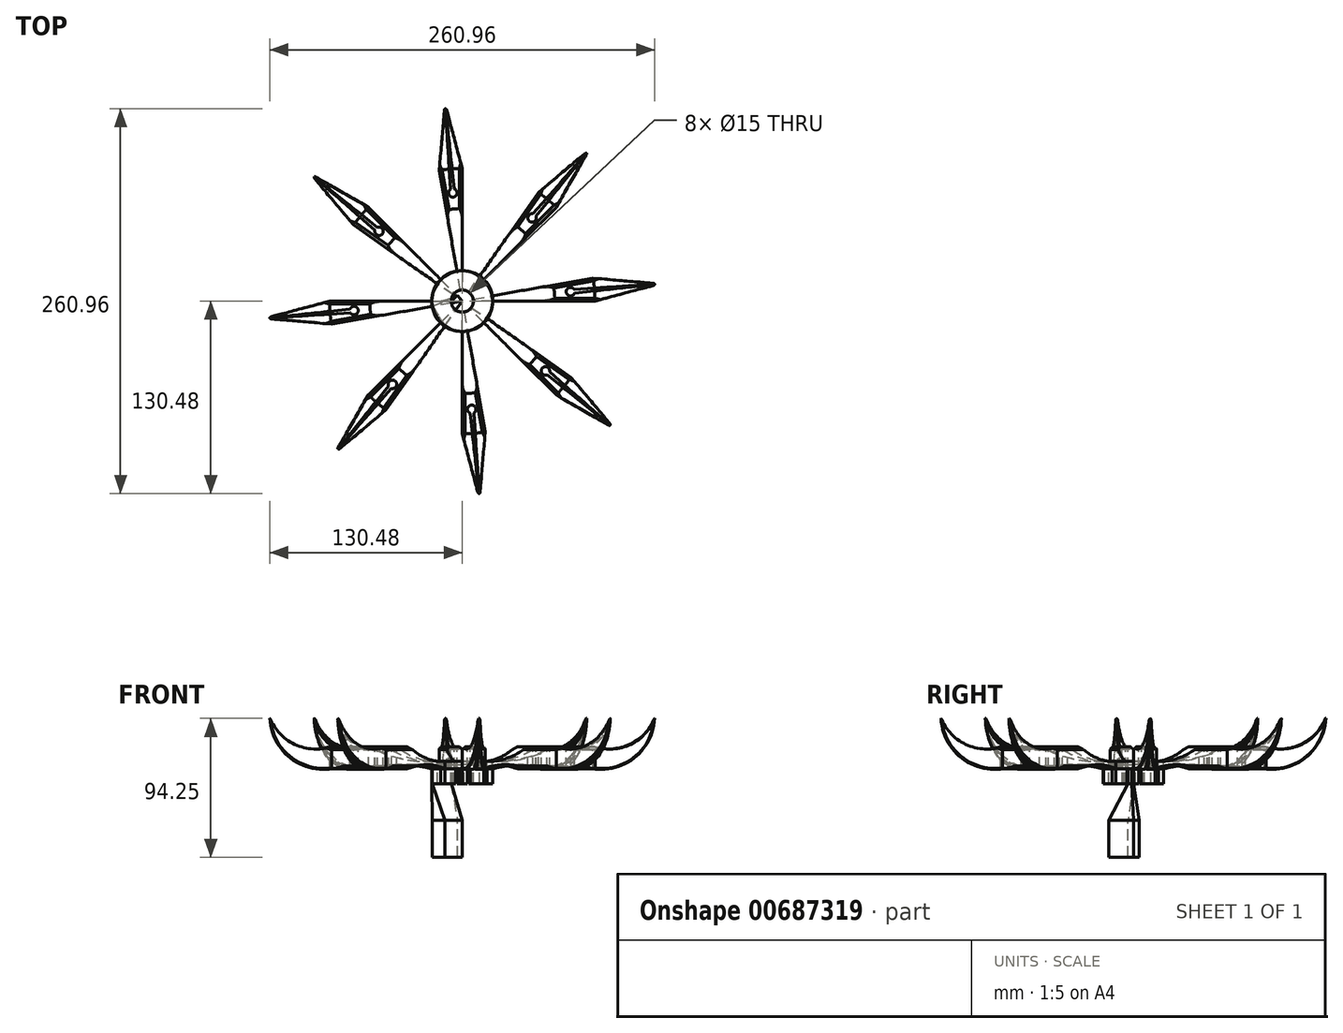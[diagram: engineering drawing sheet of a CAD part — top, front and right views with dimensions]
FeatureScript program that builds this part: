
annotation { "Feature Type Name" : "Feature", "Feature Type Description" : "" }
export const myFeature = defineFeature(function(context is Context, id is Id, definition is map)
    precondition{}
    {
        {
            var Q0;
            Q0=qCreatedBy(makeId("Front.planeOp"),FACE);
            var sketch = newSketch(context, id + "F0", { "sketchPlane" : qUnion([Q0])});
            skLineSegment(sketch, "E0.bottom", {"start": v(0, 0) * mm, "end": v(-20.6, 0) * mm});
            skLineSegment(sketch, "E0.top", {"start": v(0, 5.02) * mm, "end": v(-20.6, 5.02) * mm});
            skLineSegment(sketch, "E0.left", {"start": v(0, 0) * mm, "end": v(0, 5.02) * mm});
            skLineSegment(sketch, "E0.right", {"start": v(-20.6, 0) * mm, "end": v(-20.6, 5.02) * mm});
            skLineSegment(sketch, "E1.bottom", {"start": v(-62.76, 0) * mm, "end": v(-90, 0) * mm});
            skLineSegment(sketch, "E1.top", {"start": v(-62.76, 15.02) * mm, "end": v(-90, 15.02) * mm});
            skLineSegment(sketch, "E1.right", {"start": v(-90, 0) * mm, "end": v(-90, 15.02) * mm});
            skArc(sketch, "E2", {"start": v(-62.76, 15.02) * mm, "mid": v(-42.37, 7.11) * mm, "end": v(-20.6, 5.02) * mm});
            skArc(sketch, "E3", {"start": v(-20.6, 0) * mm, "mid": v(-41.68, 2.83) * mm, "end": v(-62.76, 0) * mm});
            skArc(sketch, "E4", {"start": v(-130.97, 34.25) * mm, "mid": v(-114.27, 16.56) * mm, "end": v(-90, 15.02) * mm});
            skArc(sketch, "E5", {"start": v(-130.97, 34.25) * mm, "mid": v(-117.92, 8.23) * mm, "end": v(-90, 0) * mm});
            skLineSegment(sketch, "E6", {"start": v(0, 35.02) * mm, "end": v(-89.6, 35.02) * mm, "construction": true});
            skLineSegment(sketch, "E7", {"start": v(-42.37, 2.82) * mm, "end": v(-42.37, 7.11) * mm});
            skPoint(sketch, "E7.startSnap0", {"position": v(-42.37, 7.11) * mm});
            skLineSegment(sketch, "E8", {"start": v(-20.6, 0) * mm, "end": v(-20.6, -8.16) * mm, "construction": true});
            skSolve(sketch);
        }
        {
            var Q0;
            Q0=makeQuery(id+"F0.imprint","IMPRINT",FACE,{"disambiguationData":[TD([[makeQuery(id+"F0.imprint","IMPRINT",EDGE,{"derivedFrom":sQuery(id+"F0.wireOp",EDGE,"E0.bottom")}),-1.0]])]});
            var Q1;
            Q1=sQuery(id+"F0.wireOp",EDGE,"E0.left");
            revolve(context, id + "F1", {"surfaceOperationType" : NewSurfaceOperationType.NEW, "entities" : qUnion([Q0]), "axis" : qUnion([Q1]), "revolveType" : RevolveType.FULL});
        }
        {
            var Q0;
            Q0=makeQuery(id+"F0.imprint","IMPRINT",FACE,{"disambiguationData":[TD([[makeQuery(id+"F0.imprint","IMPRINT",EDGE,{"derivedFrom":sQuery(id+"F0.wireOp",EDGE,"E0.right")}),1.0]])]});
            var Q1;
            Q1=makeQuery(id+"F0.imprint","IMPRINT",FACE,{"disambiguationData":[TD([[makeQuery(id+"F0.imprint","IMPRINT",EDGE,{"derivedFrom":sQuery(id+"F0.wireOp",EDGE,"E1.bottom")}),-1.0]])]});
            var Q2;
            Q2=makeQuery(id+"F0.imprint","IMPRINT",FACE,{"disambiguationData":[TD([[makeQuery(id+"F0.imprint","IMPRINT",EDGE,{"derivedFrom":sQuery(id+"F0.wireOp",EDGE,"E1.right")}),1.0]])]});
            var Q3;
            Q3=sQuery(id+"F0.wireOp",EDGE,"E0.left");
            revolve(context, id + "F2", {"operationType" : NewBodyOperationType.ADD, "surfaceOperationType" : NewSurfaceOperationType.NEW, "entities" : qUnion([Q0, Q1, Q2]), "axis" : qUnion([Q3]), "revolveType" : RevolveType.ONE_DIRECTION, "angle" : 10 * degree});
        }
        {
            var Q0;
            Q0=makeQuery(id+"F2.opRevolve","SWEPT_FACE",FACE,{"disambiguationData":[OSD([sQuery(id+"F0.wireOp",EDGE,"E1.top")])]});
            var sketch = newSketch(context, id + "F3", { "sketchPlane" : qUnion([Q0])});
            skLineSegment(sketch, "E9", {"start": v(-90, 0) * mm, "end": v(-133.6, -11.69) * mm});
            skLineSegment(sketch, "E10", {"start": v(-88.63, -15.63) * mm, "end": v(-133.6, -11.69) * mm});
            skLineSegment(sketch, "E11", {"start": v(-133.6, -11.69) * mm, "end": v(-136.23, -41.8) * mm});
            skLineSegment(sketch, "E12", {"start": v(-88.63, -15.63) * mm, "end": v(-91.27, -45.73) * mm});
            skLineSegment(sketch, "E13", {"start": v(-136.23, -41.8) * mm, "end": v(-91.27, -45.73) * mm});
            skLineSegment(sketch, "E14", {"start": v(-90, 0) * mm, "end": v(-93.65, 13.61) * mm});
            skLineSegment(sketch, "E15", {"start": v(-93.65, 13.61) * mm, "end": v(-144.43, 0) * mm});
            skLineSegment(sketch, "E16", {"start": v(-144.43, 0) * mm, "end": v(-133.6, -11.69) * mm});
            skLineSegment(sketch, "E17", {"start": v(-90, 0) * mm, "end": v(-61.8, -10.9) * mm, "construction": true});
            skLineSegment(sketch, "E18", {"start": v(-88.63, -15.63) * mm, "end": v(-62.76, 0) * mm, "construction": true});
            skCircle(sketch, "E19", {"center": v(-73.39, -6.42) * mm, "radius": 2.87 * mm});
            skLineSegment(sketch, "E20", {"start": v(-76.07, -5.39) * mm, "end": v(-133.6, -11.69) * mm});
            skLineSegment(sketch, "E21", {"start": v(-75.85, -7.9) * mm, "end": v(-133.6, -11.69) * mm});
            skSolve(sketch);
        }
        {
            var Q0;
            {var subQ0=sQuery(id+"F3.wireOp",EDGE,"E19");var subQ1=makeQuery(id+"F3.imprint","INTERSECT",VERTEX,{"derivedFrom":[subQ0,sQuery(id+"F3.wireOp",EDGE,"E20")]});Q0=makeQuery(id+"F3.imprint","IMPRINT",FACE,{"disambiguationData":[TD([[makeQuery(id+"F3.imprint","IMPRINT",EDGE,{"disambiguationData":[TD([[subQ1,-1.0]])],"derivedFrom":subQ0}),1.0]])]});}
            var Q1;
            {var subQ0=sQuery(id+"F3.wireOp",EDGE,"E20");var subQ1=sQuery(id+"F3.wireOp",EDGE,"E19");var subQ2=makeQuery(id+"F3.imprint","INTERSECT",VERTEX,{"derivedFrom":[subQ1,subQ0]});Q1=makeQuery(id+"F3.imprint","IMPRINT",FACE,{"disambiguationData":[TD([[makeQuery(id+"F3.imprint","IMPRINT",EDGE,{"disambiguationData":[TD([[subQ2,-1.0]])],"derivedFrom":subQ1}),-1.0]])]});}
            var Q2;
            {var subQ1=sQuery(id+"F3.wireOp",EDGE,"E20");var subQ3=makeQuery(id+"F2.opRevolve","SWEPT_EDGE",EDGE,{"disambiguationData":[OSD([sQuery(id+"F0.wireOp",EDGE,"E1.top"),sQuery(id+"F0.wireOp",EDGE,"E1.right"),sQuery(id+"F0.wireOp",EDGE,"E4")])]});var subQ4=makeQuery(id+"F3.imprint","INTERSECT",VERTEX,{"derivedFrom":[subQ3,subQ1]});Q2=makeQuery(id+"F3.imprint","IMPRINT",FACE,{"disambiguationData":[TD([[makeQuery(id+"F3.imprint","IMPRINT",EDGE,{"disambiguationData":[TD([[subQ4,-1.0]])],"derivedFrom":subQ1}),1.0]])]});}
            var Q3;
            Q3=makeQuery(id+"F3.imprint","IMPRINT",FACE,{"disambiguationData":[TD([[makeQuery(id+"F3.imprint","IMPRINT",EDGE,{"derivedFrom":sQuery(id+"F3.wireOp",EDGE,"E9")}),-1.0]])]});
            var Q4;
            Q4=makeQuery(id+"F3.imprint","IMPRINT",FACE,{"disambiguationData":[TD([[makeQuery(id+"F3.imprint","IMPRINT",EDGE,{"derivedFrom":sQuery(id+"F3.wireOp",EDGE,"E10")}),1.0]])]});
            extrude(context, id + "F4", {"entities" : qUnion([Q0, Q1, Q2, Q3, Q4]), "operationType" : NewBodyOperationType.REMOVE, "endBound" : BoundingType.SYMMETRIC, "oppositeDirection" : true, "depth" : 50 * mm, "offsetDistance" : 25 * mm});
        }
        {
            var Q0;
            Q0=makeQuery(id+"F2.opRevolve","CAP_EDGE",EDGE,{"disambiguationData":[OSD([sQuery(id+"F0.wireOp",EDGE,"E1.top")])],"isStart":false});
            var Q1;
            Q1=makeQuery(id+"F2.opRevolve","CAP_EDGE",EDGE,{"disambiguationData":[OSD([sQuery(id+"F0.wireOp",EDGE,"E1.top")])],"isStart":true});
            var Q2;
            Q2=makeQuery(id+"F2.opRevolve","CAP_EDGE",EDGE,{"disambiguationData":[OSD([sQuery(id+"F0.wireOp",EDGE,"E1.bottom")])],"isStart":false});
            var Q3;
            Q3=makeQuery(id+"F2.opRevolve","CAP_EDGE",EDGE,{"disambiguationData":[OSD([sQuery(id+"F0.wireOp",EDGE,"E1.bottom")])],"isStart":true});
            chamfer(context, id + "F5", {"entities" : qUnion([Q0, Q1, Q2, Q3]), "width" : 2 * mm, "tangentPropagation" : true});
        }
        {
            var Q0;
            Q0=makeQuery(id+"F4.boolean.opBoolean","INTERSECT",EDGE,{"derivedFrom":[makeQuery(id+"F2.opRevolve","SWEPT_FACE",FACE,{"disambiguationData":[OSD([sQuery(id+"F0.wireOp",EDGE,"E5")])]}),makeQuery(id+"F4.opExtrude","SWEPT_FACE",FACE,{"disambiguationData":[OSD([sQuery(id+"F3.wireOp",EDGE,"E10")])]})]});
            var Q1;
            Q1=makeQuery(id+"F4.boolean.opBoolean","INTERSECT",EDGE,{"derivedFrom":[makeQuery(id+"F2.opRevolve","SWEPT_FACE",FACE,{"disambiguationData":[OSD([sQuery(id+"F0.wireOp",EDGE,"E5")])]}),makeQuery(id+"F4.opExtrude","SWEPT_FACE",FACE,{"disambiguationData":[OSD([sQuery(id+"F3.wireOp",EDGE,"E9")])]})]});
            chamfer(context, id + "F6", {"entities" : qUnion([Q0, Q1]), "width" : .5 * mm, "tangentPropagation" : true});
        }
        {
            var Q0;
            Q0=makeQuery(id+"F1.opRevolve","SWEPT_BODY",BODY,{"disambiguationData":[OSD([sQuery(id+"F0.wireOp",EDGE,"E0.bottom"),sQuery(id+"F0.wireOp",EDGE,"E0.top"),sQuery(id+"F0.wireOp",EDGE,"E0.left"),sQuery(id+"F0.wireOp",EDGE,"E0.right")])]});
            var Q1;
            Q1=sQuery(id+"F0.wireOp",EDGE,"E0.left");
            circularPattern(context, id + "F7", {"entities" : qUnion([Q0]), "axis" : qUnion([Q1]), "angle" : 360 * degree, "instanceCount" : 8, "equalSpace" : true});
        }
        {
            var Q0;
            Q0=makeQuery(id+"F7.opPattern","COPY",FACE,{"derivedFrom":makeQuery(id+"F1.opRevolve","SWEPT_FACE",FACE,{"disambiguationData":[OSD([sQuery(id+"F0.wireOp",EDGE,"E0.bottom")])]}),"instanceName":"3"});
            var sketch = newSketch(context, id + "F8", { "sketchPlane" : qUnion([Q0])});
            skCircle(sketch, "E22", {"center": v(0, 0) * mm, "radius": 7.5 * mm});
            skSolve(sketch);
        }
        {
            var Q0;
            Q0=makeQuery(id+"F8.imprint","IMPRINT",FACE,{"disambiguationData":[TD([[makeQuery(id+"F8.imprint","IMPRINT",EDGE,{"derivedFrom":sQuery(id+"F8.wireOp",EDGE,"E22")}),1.0]])]});
            extrude(context, id + "F9", {"entities" : qUnion([Q0]), "operationType" : NewBodyOperationType.REMOVE, "endBound" : BoundingType.SYMMETRIC, "oppositeDirection" : true, "depth" : 25 * mm, "offsetDistance" : 25 * mm});
        }
        {
            var Q0;
            Q0=makeQuery(id+"F1.opRevolve","SWEPT_FACE",FACE,{"disambiguationData":[OSD([sQuery(id+"F0.wireOp",EDGE,"E0.bottom")])]});
            var sketch = newSketch(context, id + "F10", { "sketchPlane" : qUnion([Q0])});
            skLineSegment(sketch, "E23", {"start": v(-20.28, 3.58) * mm, "end": v(-20.6, 0) * mm});
            skLineSegment(sketch, "E24", {"start": v(-20.6, 0) * mm, "end": v(0, 0) * mm});
            skLineSegment(sketch, "E25", {"start": v(0, 0) * mm, "end": v(-20.28, 3.58) * mm});
            skSolve(sketch);
        }
        {
            var Q0;
            {var subQ0=sQuery(id+"F10.wireOp",EDGE,"E23");Q0=makeQuery(id+"F10.imprint","IMPRINT",FACE,{"disambiguationData":[TD([[makeQuery(id+"F10.imprint","IMPRINT",EDGE,{"derivedFrom":subQ0}),1.0]])]});}
            extrude(context, id + "F11", {"entities" : qUnion([Q0]), "depth" : 10 * mm, "offsetDistance" : 25 * mm});
        }
        {
            var Q0;
            Q0=makeQuery(id+"F11.opExtrude","SWEPT_BODY",BODY,{"disambiguationData":[OSD([sQuery(id+"F0.wireOp",EDGE,"E0.bottom"),sQuery(id+"F8.wireOp",EDGE,"E22"),sQuery(id+"F10.wireOp",EDGE,"E23"),sQuery(id+"F10.wireOp",EDGE,"E24"),sQuery(id+"F10.wireOp",EDGE,"E25")])]});
            var Q1;
            Q1=makeQuery(id+"F9.boolean.opBoolean","INTERSECT",EDGE,{"derivedFrom":[makeQuery(id+"F1.opRevolve","SWEPT_FACE",FACE,{"disambiguationData":[OSD([sQuery(id+"F0.wireOp",EDGE,"E0.bottom")])]}),makeQuery(id+"F9.opExtrude","SWEPT_FACE",FACE,{"disambiguationData":[OSD([sQuery(id+"F8.wireOp",EDGE,"E22")])]})]});
            circularPattern(context, id + "F12", {"entities" : qUnion([Q0]), "axis" : qUnion([Q1]), "angle" : 360 * degree, "instanceCount" : 8, "equalSpace" : true});
        }
        {
            var Q0;
            Q0=makeQuery(id+"F11.opExtrude","CAP_FACE",FACE,{"disambiguationData":[OSD([sQuery(id+"F0.wireOp",EDGE,"E0.bottom"),sQuery(id+"F8.wireOp",EDGE,"E22"),sQuery(id+"F10.wireOp",EDGE,"E23"),sQuery(id+"F10.wireOp",EDGE,"E24"),sQuery(id+"F10.wireOp",EDGE,"E25")])],"isStart":false});
            cPlane(context, id + "F13", {"entities" : qUnion([Q0]), "cplaneType" : CPlaneType.OFFSET, "offset" : 25 * mm, "width" : 150 * mm, "height" : 150 * mm});
        }
        {
            var Q0;
            Q0=qCreatedBy(id+"F13.planeOp",FACE);
            var sketch = newSketch(context, id + "F14", { "sketchPlane" : qUnion([Q0])});
            skCircle(sketch, "E26.cCircle", {"center": v(0, 0) * mm, "radius": 19.03 * mm, "construction": true});
            skLineSegment(sketch, "E26.0", {"start": v(-20.28, 3.58) * mm, "end": v(-11.81, 16.87) * mm});
            skLineSegment(sketch, "E26.1", {"start": v(-11.81, 16.87) * mm, "end": v(3.58, 20.28) * mm});
            skLineSegment(sketch, "E26.2", {"start": v(3.58, 20.28) * mm, "end": v(16.87, 11.81) * mm});
            skLineSegment(sketch, "E26.3", {"start": v(16.87, 11.81) * mm, "end": v(20.28, -3.58) * mm});
            skLineSegment(sketch, "E26.4", {"start": v(20.28, -3.58) * mm, "end": v(11.81, -16.87) * mm});
            skLineSegment(sketch, "E26.5", {"start": v(11.81, -16.87) * mm, "end": v(-3.58, -20.28) * mm});
            skLineSegment(sketch, "E26.6", {"start": v(-3.58, -20.28) * mm, "end": v(-16.87, -11.81) * mm});
            skLineSegment(sketch, "E26.7", {"start": v(-16.87, -11.81) * mm, "end": v(-20.28, 3.58) * mm});
            skPoint(sketch, "E26.0.midPoint", {"position": v(-16.05, 10.22) * mm});
            skLineSegment(sketch, "E27", {"start": v(-11.81, 16.87) * mm, "end": v(0, 0) * mm});
            skLineSegment(sketch, "E28", {"start": v(-20.28, 3.58) * mm, "end": v(-3.25, -3.89) * mm});
            skLineSegment(sketch, "E29", {"start": v(-3.25, -3.89) * mm, "end": v(0, 0) * mm});
            skSolve(sketch);
        }
        {
            var Q0;
            Q0=makeQuery(id+"F14.imprint","IMPRINT",FACE,{"disambiguationData":[TD([[makeQuery(id+"F14.imprint","IMPRINT",EDGE,{"derivedFrom":sQuery(id+"F14.wireOp",EDGE,"E26.0")}),-1.0]])]});
            extrude(context, id + "F15", {"entities" : qUnion([Q0]), "depth" : 25 * mm, "offsetDistance" : 25 * mm});
        }
        {
            var Q0;
            Q0=makeQuery(id+"F11.opExtrude","CAP_FACE",FACE,{"disambiguationData":[OSD([sQuery(id+"F0.wireOp",EDGE,"E0.bottom"),sQuery(id+"F8.wireOp",EDGE,"E22"),sQuery(id+"F10.wireOp",EDGE,"E23"),sQuery(id+"F10.wireOp",EDGE,"E24"),sQuery(id+"F10.wireOp",EDGE,"E25")])],"isStart":false});
            var Q1;
            Q1=makeQuery(id+"F15.opExtrude","CAP_FACE",FACE,{"disambiguationData":[OSD([sQuery(id+"F14.wireOp",EDGE,"E26.0"),sQuery(id+"F14.wireOp",EDGE,"E27"),sQuery(id+"F14.wireOp",EDGE,"E28"),sQuery(id+"F14.wireOp",EDGE,"E29")])],"isStart":true});
            loft(context, id + "F16", {"sheetProfilesArray" : [{ "sheetProfileEntities" : qUnion([Q0]) }, { "sheetProfileEntities" : qUnion([Q1]) }]});
        }
    });
